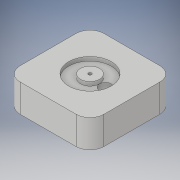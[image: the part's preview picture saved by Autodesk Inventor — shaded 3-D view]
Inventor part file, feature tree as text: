
AUTODESK INVENTOR PART (.ipt)
format: ipt  version: 2019 (Build 230136000, 136)  size: 151,552 bytes
history: native  units: in
note: dims shown in document units (in); Inventor stores cm internally (conversion verified against a paired STEP export)
features: extrude x6, sketch x6, fillet x1
ambient origin geometry x8: Origin, YZ Plane, XZ Plane, XY Plane, X Axis, Y Axis, Z Axis, Center Point
bodies: Solid1 (feature_tree)
feature tree (13):
  extrude  "Extrusion1"  Depth=0.75in
  extrude  "Extrusion2"  Depth=0.375in
  extrude  "Extrusion3"  Depth=0.5in
  extrude  "Extrusion4"  Depth=0.25in
  extrude  "Extrusion5"  Depth=0.5in TaperAngle=0.0deg
  extrude  "Extrusion6"  Depth=0.125in
  fillet  "Fillet1"  Radius=0.035in
  sketch  "Sketch1"  dims[d0=0.75in d1=0.75in]
  sketch  "Sketch2"  dims[d2=0.375in d3=0.375in]
  sketch  "Sketch3"  dims[d4=0.75in d5=0.0in d6=0.5in]
  sketch  "Sketch4"  dims[d7=0.5in d8=0.25in]
  sketch  "Sketch5"  dims[d9=0.25in d10=0.5in d11=0.0in]
  sketch  "Sketch7"  dims[d12=0.38in d13=0.17in d14=0.035in d15=0.0in d16=0.0285in d17=0.035in d18=0.0in d19=0.105in d20=0.1375in d21=0.035in d22=0.0in d23=0.5in d24=0.75in d25=0.035in d26=0.0in d27=0.125in]
